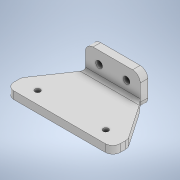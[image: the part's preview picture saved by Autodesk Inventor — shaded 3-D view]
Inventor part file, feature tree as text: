
AUTODESK INVENTOR PART (.ipt)
format: ipt  version: 2020 (Build 240168000, 168)  size: 177,152 bytes
history: native  units: in
note: dims shown in document units (in); Inventor stores cm internally (conversion verified against a paired STEP export)
features: fillet x4, extrude x3, sketch x3
ambient origin geometry x8: Origin, YZ Plane, XZ Plane, XY Plane, X Axis, Y Axis, Z Axis, Center Point
bodies: Solid1 (feature_tree)
feature tree (10):
  extrude  "Extrusion1"  Depth=0.6299in
  extrude  "Extrusion2"  Depth=0.1969in
  extrude  "Extrusion3"  Depth=0.1969in
  fillet  "Fillet1"  [1 undecoded]
  fillet  "Fillet2"  Radius=0.7087in
  fillet  "Fillet3"  Radius=0.3543in
  fillet  "Fillet4"  Radius=0.1969in
  sketch  "Sketch1"  dims[d0=1.4173in d1=0.6299in]
  sketch  "Sketch2"  dims[d2=0.1969in d3=0.0in d4=0.1772in]
  sketch  "Sketch3"  dims[d5=0.1772in d6=0.315in d7=0.0in d8=0.7087in d9=0.3543in d10=0.1969in d11=0.0in d12=1.5748in d13=2.7559in d14=0.3937in d15=0.3937in d16=0.6693in d17=0.1378in d18=0.1378in d19=1.7638in d20=0.0in d21=0.1732in d22=1.2598in d23=0.1969in d24=0.0in d25=0.0787in d26=0.1969in d27=0.1969in d28=0.1969in]
note: 1 required parameter value undecoded (feature->parameter linkage not recoverable at this tier; creation-order binding heuristic only, values carry confidence <= 0.55)
